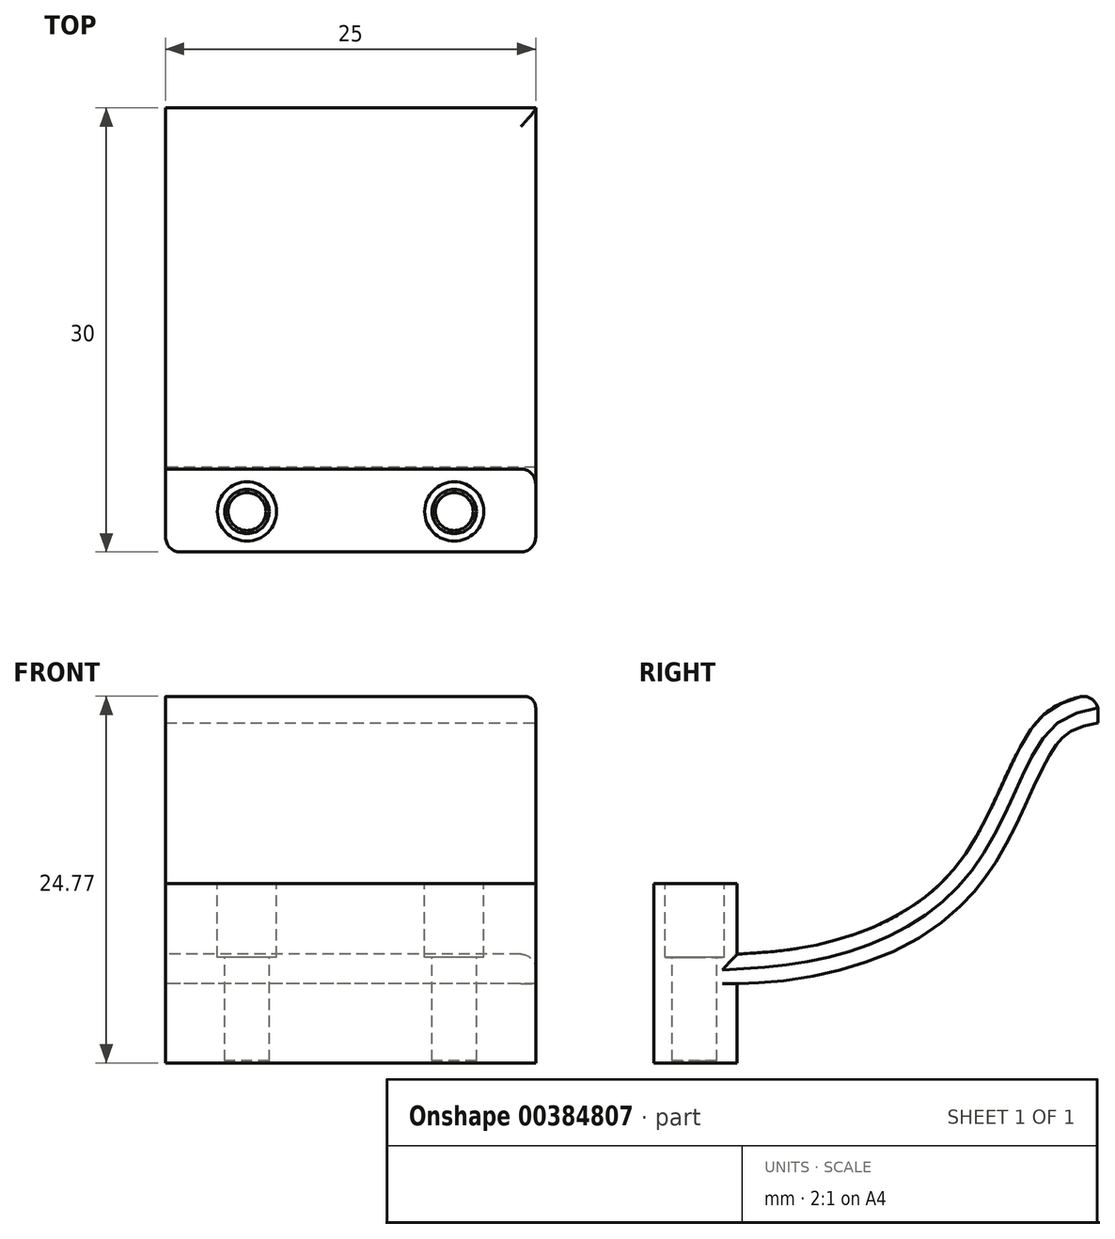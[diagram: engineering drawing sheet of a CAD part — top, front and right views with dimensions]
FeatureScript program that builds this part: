
annotation { "Feature Type Name" : "Feature", "Feature Type Description" : "" }
export const myFeature = defineFeature(function(context is Context, id is Id, definition is map)
    precondition{}
    {
        {
            var Q0;
            Q0=qCreatedBy(makeId("Top.planeOp"),FACE);
            var sketch = newSketch(context, id + "F0", { "sketchPlane" : qUnion([Q0])});
            skLineSegment(sketch, "E0.bottom", {"start": v(12.5, 15) * mm, "end": v(-12.5, 15) * mm});
            skLineSegment(sketch, "E0.top", {"start": v(12.5, -15) * mm, "end": v(-12.5, -15) * mm});
            skLineSegment(sketch, "E0.left", {"start": v(12.5, 15) * mm, "end": v(12.5, -15) * mm});
            skLineSegment(sketch, "E0.right", {"start": v(-12.5, 15) * mm, "end": v(-12.5, -15) * mm});
            skPoint(sketch, "E0.middle", {"position": v(0, 0) * mm});
            skLineSegment(sketch, "E1", {"start": v(-12.5, 15) * mm, "end": v(12.5, -15) * mm});
            skLineSegment(sketch, "E2.0", {"start": v(-12.5, 7.19) * mm, "end": v(6, -15) * mm});
            skLineSegment(sketch, "E3.0", {"start": v(-12.5, -0.62) * mm, "end": v(-0.52, -15) * mm});
            skLineSegment(sketch, "E4.0", {"start": v(-12.5, -8.43) * mm, "end": v(-7.03, -15) * mm});
            skLineSegment(sketch, "E5.0", {"start": v(-6, 15) * mm, "end": v(12.5, -7.19) * mm});
            skLineSegment(sketch, "E6.0", {"start": v(0.52, 15) * mm, "end": v(12.5, 0.62) * mm});
            skLineSegment(sketch, "E7.0", {"start": v(7.03, 15) * mm, "end": v(12.5, 8.43) * mm});
            skLineSegment(sketch, "E8.0", {"start": v(-12.5, 11.1) * mm, "end": v(9.25, -15) * mm});
            skLineSegment(sketch, "E9.0", {"start": v(-12.5, 3.28) * mm, "end": v(2.74, -15) * mm});
            skLineSegment(sketch, "E10.0", {"start": v(-12.5, -4.53) * mm, "end": v(-3.77, -15) * mm});
            skLineSegment(sketch, "E11.0", {"start": v(-9.25, 15) * mm, "end": v(12.5, -11.1) * mm});
            skLineSegment(sketch, "E12.0", {"start": v(-2.74, 15) * mm, "end": v(12.5, -3.28) * mm});
            skLineSegment(sketch, "E13.0", {"start": v(3.77, 15) * mm, "end": v(12.5, 4.53) * mm});
            skLineSegment(sketch, "E14.0", {"start": v(10.28, 15) * mm, "end": v(12.5, 12.34) * mm});
            skSolve(sketch);
        }
        {
            var Q0;
            Q0=makeQuery(id+"F0.imprint","IMPRINT",FACE,{"disambiguationData":[TD([[makeQuery(id+"F0.imprint","IMPRINT",EDGE,{"derivedFrom":sQuery(id+"F0.wireOp",EDGE,"E0.bottom")}),1.0]])]});
            var Q1;
            {var subQ0=sQuery(id+"F0.wireOp",EDGE,"E7.0");Q1=makeQuery(id+"F0.imprint","IMPRINT",FACE,{"disambiguationData":[TD([[makeQuery(id+"F0.imprint","IMPRINT",EDGE,{"derivedFrom":subQ0}),1.0]])]});}
            var Q2;
            {var subQ0=sQuery(id+"F0.wireOp",EDGE,"E7.0");Q2=makeQuery(id+"F0.imprint","IMPRINT",FACE,{"disambiguationData":[TD([[makeQuery(id+"F0.imprint","IMPRINT",EDGE,{"derivedFrom":subQ0}),-1.0]])]});}
            var Q3;
            {var subQ0=sQuery(id+"F0.wireOp",EDGE,"E6.0");Q3=makeQuery(id+"F0.imprint","IMPRINT",FACE,{"disambiguationData":[TD([[makeQuery(id+"F0.imprint","IMPRINT",EDGE,{"derivedFrom":subQ0}),1.0]])]});}
            var Q4;
            {var subQ0=sQuery(id+"F0.wireOp",EDGE,"E6.0");Q4=makeQuery(id+"F0.imprint","IMPRINT",FACE,{"disambiguationData":[TD([[makeQuery(id+"F0.imprint","IMPRINT",EDGE,{"derivedFrom":subQ0}),-1.0]])]});}
            var Q5;
            {var subQ0=sQuery(id+"F0.wireOp",EDGE,"E5.0");Q5=makeQuery(id+"F0.imprint","IMPRINT",FACE,{"disambiguationData":[TD([[makeQuery(id+"F0.imprint","IMPRINT",EDGE,{"derivedFrom":subQ0}),1.0]])]});}
            var Q6;
            {var subQ0=sQuery(id+"F0.wireOp",EDGE,"E5.0");Q6=makeQuery(id+"F0.imprint","IMPRINT",FACE,{"disambiguationData":[TD([[makeQuery(id+"F0.imprint","IMPRINT",EDGE,{"derivedFrom":subQ0}),-1.0]])]});}
            var Q7;
            {var subQ0=sQuery(id+"F0.wireOp",EDGE,"E1");Q7=makeQuery(id+"F0.imprint","IMPRINT",FACE,{"disambiguationData":[TD([[makeQuery(id+"F0.imprint","IMPRINT",EDGE,{"derivedFrom":subQ0}),-1.0]])]});}
            var Q8;
            {var subQ0=sQuery(id+"F0.wireOp",EDGE,"E2.0");Q8=makeQuery(id+"F0.imprint","IMPRINT",FACE,{"disambiguationData":[TD([[makeQuery(id+"F0.imprint","IMPRINT",EDGE,{"derivedFrom":subQ0}),-1.0]])]});}
            var Q9;
            {var subQ0=sQuery(id+"F0.wireOp",EDGE,"E3.0");Q9=makeQuery(id+"F0.imprint","IMPRINT",FACE,{"disambiguationData":[TD([[makeQuery(id+"F0.imprint","IMPRINT",EDGE,{"derivedFrom":subQ0}),-1.0]])]});}
            var Q10;
            {var subQ0=sQuery(id+"F0.wireOp",EDGE,"E4.0");Q10=makeQuery(id+"F0.imprint","IMPRINT",FACE,{"disambiguationData":[TD([[makeQuery(id+"F0.imprint","IMPRINT",EDGE,{"derivedFrom":subQ0}),1.0]])]});}
            var Q11;
            {var subQ3=sQuery(id+"F0.wireOp",EDGE,"E4.0");Q11=makeQuery(id+"F0.imprint","IMPRINT",FACE,{"disambiguationData":[TD([[makeQuery(id+"F0.imprint","IMPRINT",EDGE,{"derivedFrom":subQ3}),-1.0]])]});}
            var Q12;
            {var subQ0=sQuery(id+"F0.wireOp",EDGE,"E1");Q12=makeQuery(id+"F0.imprint","IMPRINT",FACE,{"disambiguationData":[TD([[makeQuery(id+"F0.imprint","IMPRINT",EDGE,{"derivedFrom":subQ0}),1.0]])]});}
            var Q13;
            {var subQ0=sQuery(id+"F0.wireOp",EDGE,"E2.0");Q13=makeQuery(id+"F0.imprint","IMPRINT",FACE,{"disambiguationData":[TD([[makeQuery(id+"F0.imprint","IMPRINT",EDGE,{"derivedFrom":subQ0}),1.0]])]});}
            var Q14;
            {var subQ0=sQuery(id+"F0.wireOp",EDGE,"E3.0");Q14=makeQuery(id+"F0.imprint","IMPRINT",FACE,{"disambiguationData":[TD([[makeQuery(id+"F0.imprint","IMPRINT",EDGE,{"derivedFrom":subQ0}),1.0]])]});}
            extrude(context, id + "F1", {"entities" : qUnion([Q0, Q1, Q2, Q3, Q4, Q5, Q6, Q7, Q8, Q9, Q10, Q11, Q12, Q13, Q14]), "depth" : 25 * mm});
        }
        {
            var Q0;
            Q0=makeQuery(id+"F1.opExtrude","SWEPT_FACE",FACE,{"disambiguationData":[OSD([sQuery(id+"F0.wireOp",EDGE,"E0.right")])]});
            var sketch = newSketch(context, id + "F2", { "sketchPlane" : qUnion([Q0])});
            skFitSpline(sketch, "E15", {"points": [v(-15, 25) * mm, v(-10.94, 23.14) * mm, v(-5.5, 13.36) * mm, v(3.14, 8.18) * mm, v(9.39, 7.35) * mm], "startDerivative": vector(22.84, -4.4) * mm, "endDerivative": vector(26.28, -1.59) * mm});
            skLineSegment(sketch, "E16", {"start": v(9.39, 7.35) * mm, "end": v(9.39, 12.13) * mm});
            skLineSegment(sketch, "E17", {"start": v(9.39, 12.13) * mm, "end": v(15, 12.13) * mm});
            skFitSpline(sketch, "E18.0", {"points": [v(-15.38, 23.04) * mm, v(-14.9, 22.94) * mm, v(-14.27, 22.82) * mm, v(-13.6, 22.6) * mm, v(-13.17, 22.4) * mm, v(-12.87, 22.21) * mm, v(-12.63, 22.01) * mm, v(-12.46, 21.84) * mm, v(-12.27, 21.62) * mm, v(-12.07, 21.35) * mm, v(-11.86, 21.02) * mm, v(-11.56, 20.51) * mm, v(-11.18, 19.78) * mm, v(-10.7, 18.77) * mm, v(-10.2, 17.66) * mm, v(-9.65, 16.5) * mm, v(-9.06, 15.29) * mm, v(-8.4, 14.08) * mm, v(-7.78, 13.09) * mm, v(-7.23, 12.32) * mm, v(-6.63, 11.57) * mm, v(-5.83, 10.72) * mm, v(-4.47, 9.52) * mm, v(-2.65, 8.3) * mm, v(-0.4, 7.2) * mm, v(1.83, 6.43) * mm, v(3.9, 5.93) * mm, v(6.45, 5.52) * mm, v(8.17, 5.42) * mm, v(9.27, 5.35) * mm]});
            skLineSegment(sketch, "E19", {"start": v(9.39, 7.35) * mm, "end": v(9.39, 0) * mm});
            skLineSegment(sketch, "E20", {"start": v(9.27, 5.35) * mm, "end": v(9.39, 5.35) * mm});
            skLineSegment(sketch, "E21", {"start": v(-15, 25) * mm, "end": v(-15, 22.96) * mm});
            skSolve(sketch);
        }
        {
            var Q0;
            Q0=makeQuery(id+"F2.imprint","IMPRINT",FACE,{"disambiguationData":[TD([[makeQuery(id+"F2.imprint","IMPRINT",EDGE,{"derivedFrom":sQuery(id+"F2.wireOp",EDGE,"E15")}),1.0]])]});
            var Q1;
            {var subQ4=sQuery(id+"F2.wireOp",EDGE,"E18.0");Q1=makeQuery(id+"F2.imprint","IMPRINT",FACE,{"disambiguationData":[TD([[makeQuery(id+"F2.imprint","IMPRINT",EDGE,{"derivedFrom":subQ4}),-1.0]])]});}
            extrude(context, id + "F3", {"entities" : qUnion([Q0, Q1]), "operationType" : NewBodyOperationType.REMOVE, "endBound" : BoundingType.THROUGH_ALL, "oppositeDirection" : true, "depth" : 25 * mm});
        }
        {
            var Q0;
            Q0=makeQuery(id+"F3.boolean.opBoolean","COPY",FACE,{"derivedFrom":makeQuery(id+"F3.opExtrude","SWEPT_FACE",FACE,{"disambiguationData":[OSD([sQuery(id+"F2.wireOp",EDGE,"E17")])]})});
            var sketch = newSketch(context, id + "F4", { "sketchPlane" : qUnion([Q0])});
            skCircle(sketch, "E22", {"center": v(-7, -12.26) * mm, "radius": 1.3 * mm});
            skCircle(sketch, "E23", {"center": v(7, -12.26) * mm, "radius": 1.3 * mm});
            skSolve(sketch);
        }
        {
            var Q0;
            Q0=sQuery(id+"F4.wireOp",VERTEX,"E22.center");
            var Q1;
            Q1=sQuery(id+"F4.wireOp",VERTEX,"E23.center");
            var Q2;
            Q2=makeQuery(id+"F1.opExtrude","SWEPT_BODY",BODY,{"disambiguationData":[OSD([sQuery(id+"F0.wireOp",EDGE,"E0.bottom"),sQuery(id+"F0.wireOp",EDGE,"E0.top"),sQuery(id+"F0.wireOp",EDGE,"E0.left"),sQuery(id+"F0.wireOp",EDGE,"E0.right")])]});
            hole(context, id + "F5", {"style" : HoleStyle.C_BORE, "endStyle" : HoleEndStyle.BLIND, "holeDiameter" : 3 * mm, "cBoreDiameter" : 4 * mm, "cBoreDepth" : 5 * mm, "holeDepth" : 12 * mm, "isTappedThrough" : true, "tappedDepth" : 12 * mm, "tapClearance" : 3, "locations" : qUnion([Q0, Q1]), "scope" : qUnion([Q2])});
        }
        {
            var Q0;
            Q0=makeQuery(id+"F1.opExtrude","SWEPT_EDGE",EDGE,{"disambiguationData":[OSD([sQuery(id+"F0.wireOp",EDGE,"E0.top"),sQuery(id+"F0.wireOp",EDGE,"E0.left")])]});
            var Q1;
            Q1=makeQuery(id+"F1.opExtrude","SWEPT_EDGE",EDGE,{"disambiguationData":[OSD([sQuery(id+"F0.wireOp",EDGE,"E0.top"),sQuery(id+"F0.wireOp",EDGE,"E0.right")])]});
            var Q2;
            Q2=makeQuery(id+"F3.boolean.opBoolean","INTERSECT",EDGE,{"derivedFrom":[makeQuery(id+"F1.opExtrude","SWEPT_FACE",FACE,{"disambiguationData":[OSD([sQuery(id+"F0.wireOp",EDGE,"E0.left")])]}),makeQuery(id+"F3.opExtrude","SWEPT_FACE",FACE,{"disambiguationData":[OSD([sQuery(id+"F2.wireOp",EDGE,"E15")])]})]});
            var Q3;
            Q3=makeQuery(id+"F3.boolean.opBoolean","COPY",EDGE,{"derivedFrom":makeQuery(id+"F3.opExtrude","CAP_EDGE",EDGE,{"disambiguationData":[OSD([sQuery(id+"F2.wireOp",EDGE,"E15")])],"isStart":true})});
            var Q4;
            Q4=makeQuery(id+"F3.boolean.opBoolean","INTERSECT",EDGE,{"derivedFrom":[makeQuery(id+"F1.opExtrude","SWEPT_FACE",FACE,{"disambiguationData":[OSD([sQuery(id+"F0.wireOp",EDGE,"E0.left")])]}),makeQuery(id+"F3.opExtrude","SWEPT_FACE",FACE,{"disambiguationData":[OSD([sQuery(id+"F2.wireOp",EDGE,"E16")])]})]});
            var Q5;
            Q5=makeQuery(id+"F3.boolean.opBoolean","COPY",EDGE,{"derivedFrom":makeQuery(id+"F3.opExtrude","CAP_EDGE",EDGE,{"disambiguationData":[OSD([sQuery(id+"F2.wireOp",EDGE,"E16")])],"isStart":true})});
            var Q6;
            Q6=makeQuery(id+"F3.boolean.opBoolean","MERGE",EDGE,{"derivedFrom":[makeQuery(id+"F1.opExtrude","CAP_EDGE",EDGE,{"disambiguationData":[OSD([sQuery(id+"F0.wireOp",EDGE,"E0.bottom")])],"isStart":false}),makeQuery(id+"F3.opExtrude","SWEPT_EDGE",EDGE,{"disambiguationData":[OSD([sQuery(id+"F0.wireOp",EDGE,"E0.right"),sQuery(id+"F2.wireOp",EDGE,"E15"),sQuery(id+"F2.wireOp",EDGE,"E21")])]})]});
            var Q7;
            Q7=makeQuery(id+"F3.boolean.opBoolean","INTERSECT",EDGE,{"derivedFrom":[makeQuery(id+"F1.opExtrude","SWEPT_FACE",FACE,{"disambiguationData":[OSD([sQuery(id+"F0.wireOp",EDGE,"E0.left")])]}),makeQuery(id+"F3.opExtrude","SWEPT_FACE",FACE,{"disambiguationData":[OSD([sQuery(id+"F2.wireOp",EDGE,"E19")])]})]});
            var Q8;
            Q8=makeQuery(id+"F3.boolean.opBoolean","COPY",EDGE,{"derivedFrom":makeQuery(id+"F3.opExtrude","CAP_EDGE",EDGE,{"disambiguationData":[OSD([sQuery(id+"F2.wireOp",EDGE,"E19")])],"isStart":true})});
            var Q9;
            Q9=makeQuery(id+"F3.boolean.opBoolean","COPY",EDGE,{"derivedFrom":makeQuery(id+"F3.opExtrude","SWEPT_EDGE",EDGE,{"disambiguationData":[OSD([sQuery(id+"F0.wireOp",EDGE,"E0.bottom"),sQuery(id+"F0.wireOp",EDGE,"E0.right"),sQuery(id+"F0.wireOp",EDGE,"E1"),sQuery(id+"F2.wireOp",EDGE,"E18.0")])]})});
            fillet(context, id + "F6", {"entities" : qUnion([Q0, Q1, Q2, Q3, Q4, Q5, Q6, Q7, Q8, Q9]), "radius" : 1 * mm, "tangentPropagation" : true, "allowEdgeOverflow" : false});
        }
    });
